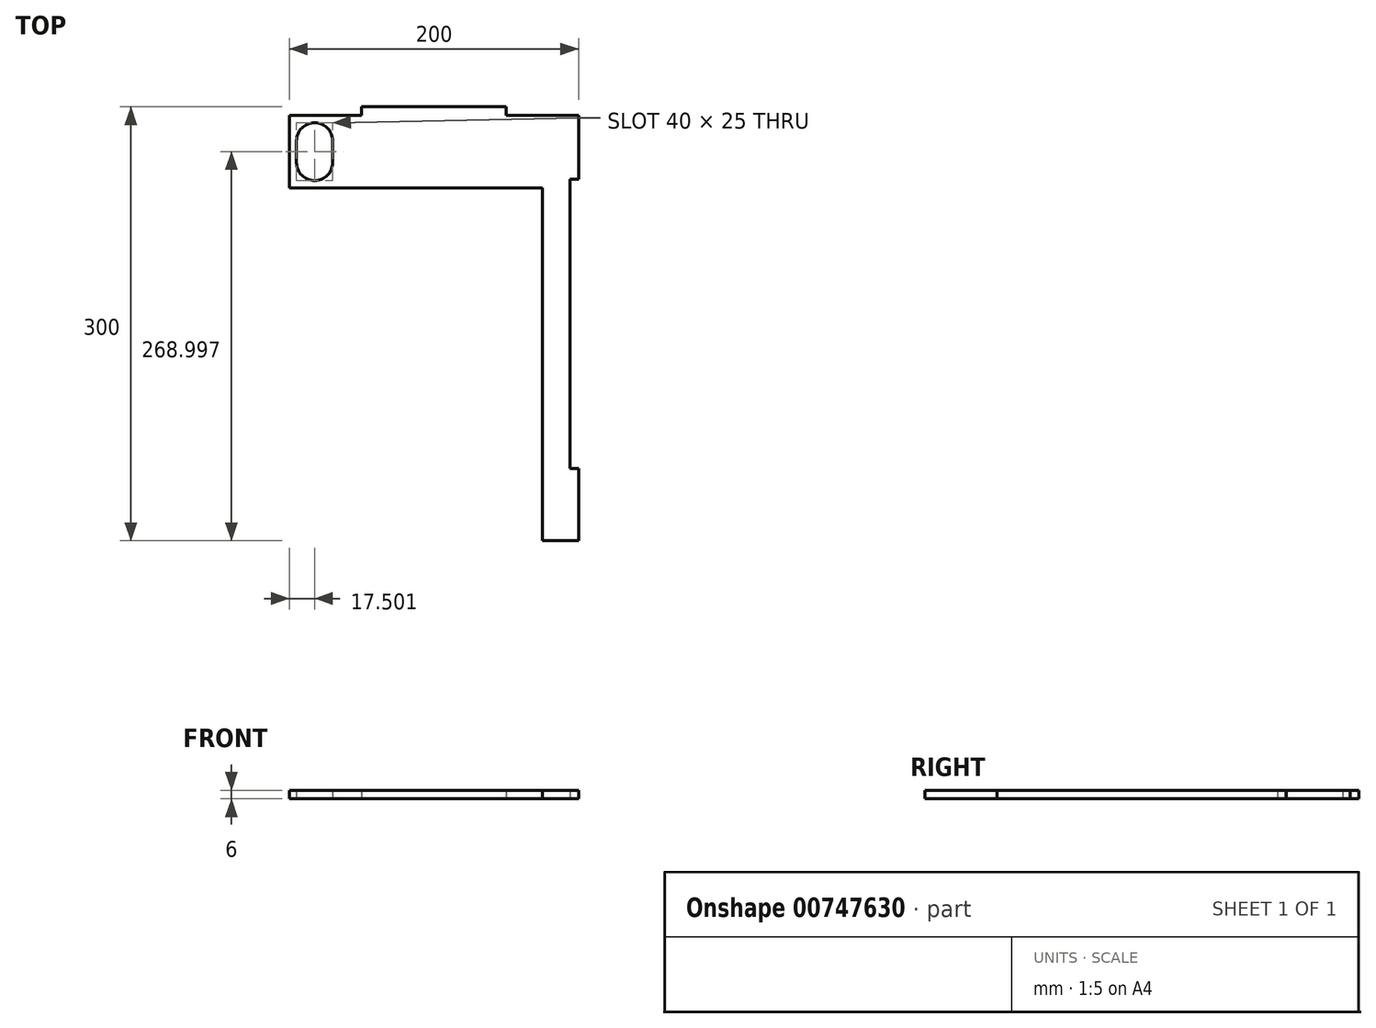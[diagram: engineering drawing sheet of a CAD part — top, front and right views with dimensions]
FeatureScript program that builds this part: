
annotation { "Feature Type Name" : "Feature", "Feature Type Description" : "" }
export const myFeature = defineFeature(function(context is Context, id is Id, definition is map)
    precondition{}
    {
        {
            var Q0;
            Q0=qCreatedBy(makeId("Top.planeOp"),FACE);
            var sketch = newSketch(context, id + "F0", { "sketchPlane" : qUnion([Q0])});
            skLineSegment(sketch, "E0.bottom", {"start": v(-49.55, 218.88) * mm, "end": v(0.45, 218.88) * mm});
            skLineSegment(sketch, "E0.top", {"start": v(125.45, -75.12) * mm, "end": v(150.45, -75.12) * mm});
            skLineSegment(sketch, "E0.left", {"start": v(-49.55, 218.88) * mm, "end": v(-49.55, 168.88) * mm});
            skLineSegment(sketch, "E0.right", {"start": v(150.45, 218.88) * mm, "end": v(150.45, 174.88) * mm});
            skLineSegment(sketch, "E1.top", {"start": v(0.45, 224.88) * mm, "end": v(100.45, 224.88) * mm});
            skLineSegment(sketch, "E1.left", {"start": v(0.45, 218.88) * mm, "end": v(0.45, 224.88) * mm});
            skLineSegment(sketch, "E1.right", {"start": v(100.45, 218.88) * mm, "end": v(100.45, 224.88) * mm});
            skLineSegment(sketch, "E2.trimOffspring", {"start": v(100.45, 218.88) * mm, "end": v(150.45, 218.88) * mm});
            skLineSegment(sketch, "E3.bottom", {"start": v(-49.55, 168.88) * mm, "end": v(125.45, 168.88) * mm});
            skLineSegment(sketch, "E3.right", {"start": v(125.45, 168.88) * mm, "end": v(125.45, -75.12) * mm});
            skLineSegment(sketch, "E4.bottom", {"start": v(150.45, 174.88) * mm, "end": v(144.45, 174.88) * mm});
            skLineSegment(sketch, "E4.top", {"start": v(150.45, -25.12) * mm, "end": v(144.45, -25.12) * mm});
            skLineSegment(sketch, "E4.right", {"start": v(144.45, 174.88) * mm, "end": v(144.45, -25.12) * mm});
            skLineSegment(sketch, "E5.trimOffspring", {"start": v(150.45, -25.12) * mm, "end": v(150.45, -75.12) * mm});
            skLineSegment(sketch, "E6.bottom", {"start": v(-44.55, 201.38) * mm, "end": v(-19.55, 201.38) * mm});
            skLineSegment(sketch, "E6.top", {"start": v(-44.55, 186.38) * mm, "end": v(-19.55, 186.38) * mm});
            skLineSegment(sketch, "E6.left", {"start": v(-44.55, 201.38) * mm, "end": v(-44.55, 186.38) * mm});
            skLineSegment(sketch, "E6.right", {"start": v(-19.55, 201.38) * mm, "end": v(-19.55, 186.38) * mm});
            skArc(sketch, "E7", {"start": v(-19.55, 201.38) * mm, "mid": v(-32.05, 213.88) * mm, "end": v(-44.55, 201.38) * mm});
            skArc(sketch, "E8", {"start": v(-44.55, 186.38) * mm, "mid": v(-32.05, 173.88) * mm, "end": v(-19.55, 186.38) * mm});
            skLineSegment(sketch, "E9", {"start": v(-32.05, 213.88) * mm, "end": v(-32.05, 218.88) * mm, "construction": true});
            skLineSegment(sketch, "E10", {"start": v(-32.05, 173.88) * mm, "end": v(-32.05, 168.88) * mm, "construction": true});
            skLineSegment(sketch, "E11", {"start": v(-44.55, 193.88) * mm, "end": v(-49.55, 193.88) * mm, "construction": true});
            skSolve(sketch);
        }
        {
            var Q0;
            Q0=makeQuery(id+"F0.imprint","IMPRINT",FACE,{"disambiguationData":[TD([[makeQuery(id+"F0.imprint","IMPRINT",EDGE,{"derivedFrom":sQuery(id+"F0.wireOp",EDGE,"E0.bottom")}),-1.0]])]});
            extrude(context, id + "F1", {"entities" : qUnion([Q0]), "depth" : 6 * mm, "offsetDistance" : 25.4 * mm});
        }
    });
